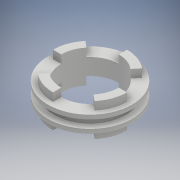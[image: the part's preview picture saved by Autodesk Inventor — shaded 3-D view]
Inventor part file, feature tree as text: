
AUTODESK INVENTOR PART (.ipt)
format: ipt  version: 2017 (Build 210142000, 142)  size: 166,400 bytes
history: native  units: mm
features: extrude x3, sketch x3, plane x1, pattern_circular x1, mirror x1
ambient origin geometry x8: Origin, YZ Plane, XZ Plane, XY Plane, X Axis, Y Axis, Z Axis, Center Point
bodies: Solid1 (feature_tree)
feature tree (9):
  extrude  "Extrusion1"  Depth=8.0mm
  plane  "Work Plane1"
  extrude  "Extrusion2"  Depth=10.0mm
  extrude  "Extrusion3"  Depth=5.0mm
  pattern_circular  "Circular Pattern1"  [2 undecoded]
  mirror  "Mirror1"
  sketch  "Sketch1"  dims[d0=35.0mm d1=8.0mm]
  sketch  "Sketch2"  dims[d2=10.0mm d3=0.0mm d4=4.0mm]
  sketch  "Sketch3"  dims[d5=5.0mm d6=0.0mm d7=5.0mm d8=6.981317mm d9=5.0mm d10=0.0mm d11=40.0mm d12=360.0deg]
note: 2 required parameter values undecoded (feature->parameter linkage not recoverable at this tier; creation-order binding heuristic only, values carry confidence <= 0.55)
